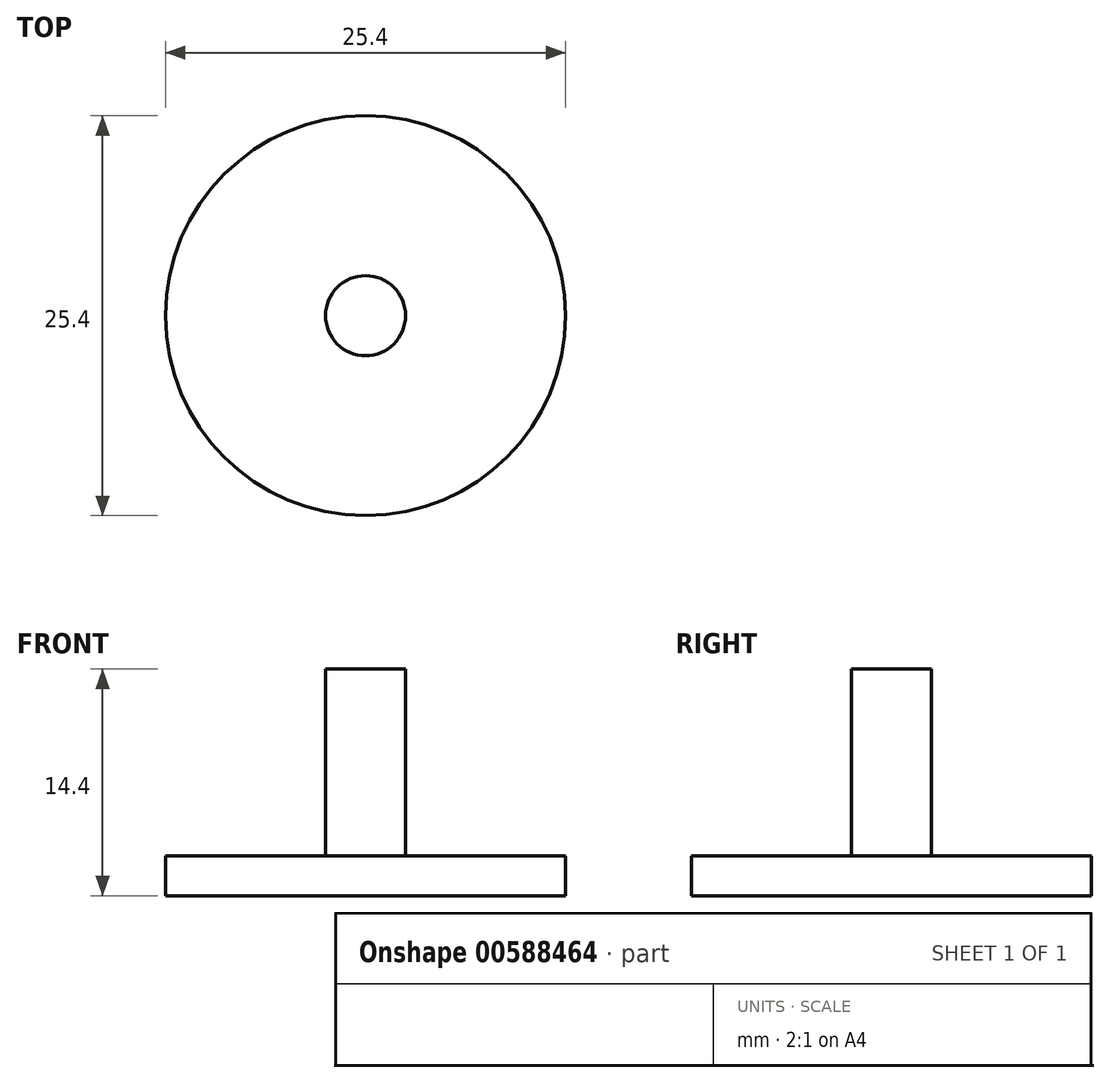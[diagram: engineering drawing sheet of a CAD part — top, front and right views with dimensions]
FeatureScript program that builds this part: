
annotation { "Feature Type Name" : "Feature", "Feature Type Description" : "" }
export const myFeature = defineFeature(function(context is Context, id is Id, definition is map)
    precondition{}
    {
        {
            var Q0;
            Q0=qCreatedBy(makeId("Front.planeOp"),FACE);
            var sketch = newSketch(context, id + "F0", { "sketchPlane" : qUnion([Q0])});
            skLineSegment(sketch, "E0.bottom", {"start": v(0, 0) * mm, "end": v(-12.7, 0) * mm});
            skLineSegment(sketch, "E0.top", {"start": v(-2.54, 2.54) * mm, "end": v(-12.7, 2.54) * mm});
            skLineSegment(sketch, "E0.left", {"start": v(0, 0) * mm, "end": v(0, 2.54) * mm});
            skLineSegment(sketch, "E0.right", {"start": v(-12.7, 0) * mm, "end": v(-12.7, 2.54) * mm});
            skLineSegment(sketch, "E1.top", {"start": v(-2.54, 14.4) * mm, "end": v(0, 14.4) * mm});
            skLineSegment(sketch, "E1.left", {"start": v(-2.54, 2.54) * mm, "end": v(-2.54, 14.4) * mm});
            skLineSegment(sketch, "E1.right", {"start": v(0, 3.68) * mm, "end": v(0, 14.4) * mm});
            skLineSegment(sketch, "E2", {"start": v(0, 2.54) * mm, "end": v(0, 3.68) * mm});
            skSolve(sketch);
        }
        {
            var Q0;
            Q0 = qSketchRegion(id + "F0", true);
            var Q1;
            Q1=sQuery(id+"F0.wireOp",EDGE,"E0.left");
            revolve(context, id + "F1", {"entities" : qUnion([Q0]), "axis" : qUnion([Q1]), "revolveType" : RevolveType.FULL});
        }
    });
